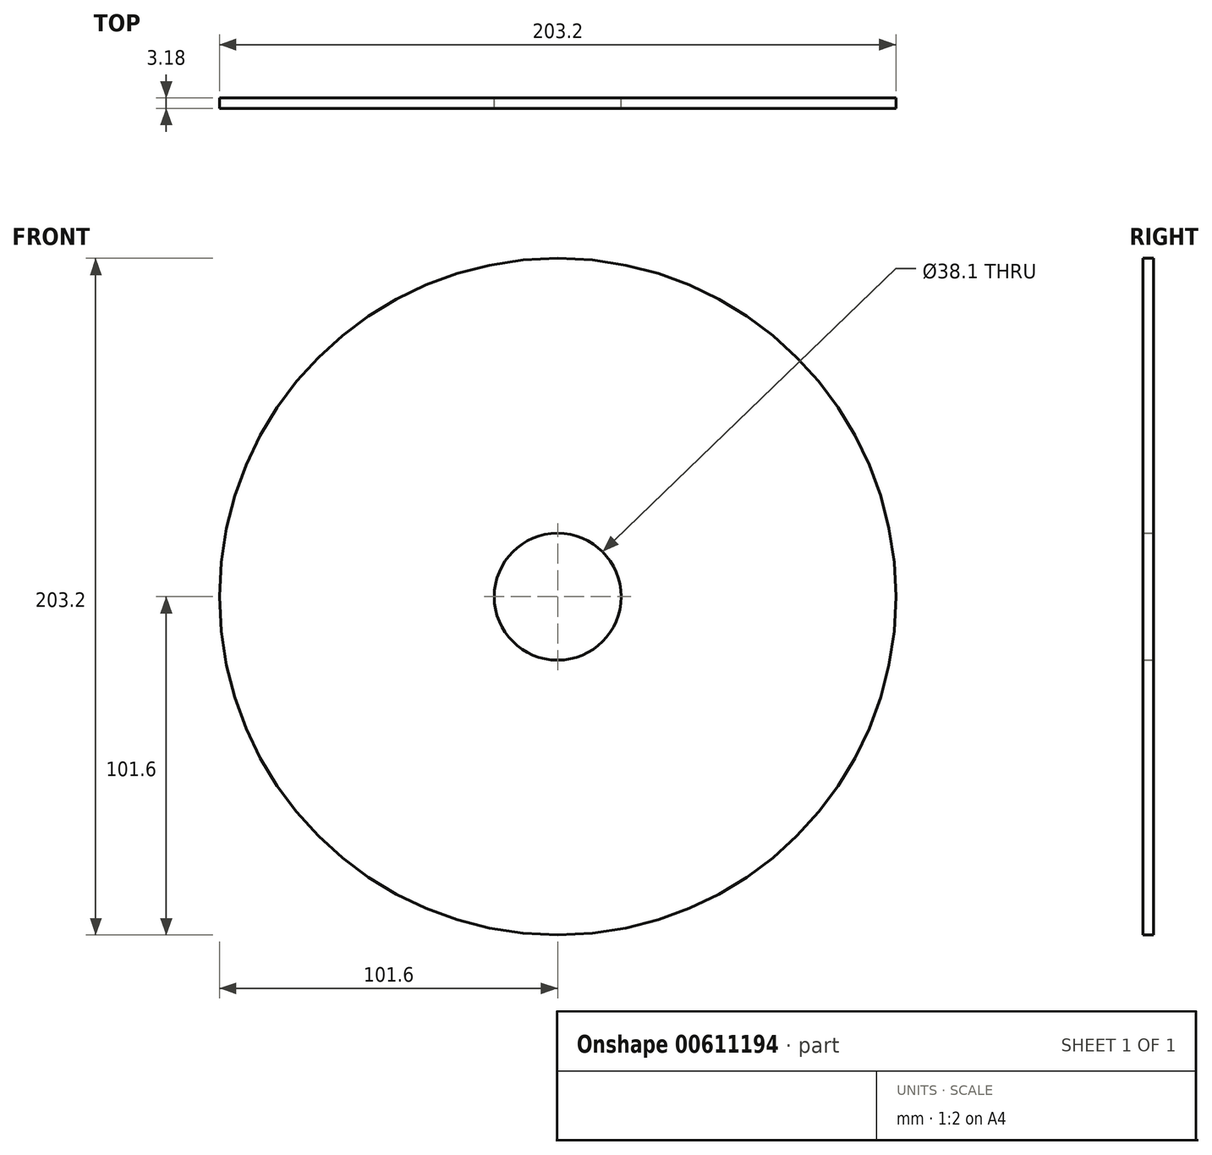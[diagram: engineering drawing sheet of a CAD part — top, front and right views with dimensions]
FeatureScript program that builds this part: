
annotation { "Feature Type Name" : "Feature", "Feature Type Description" : "" }
export const myFeature = defineFeature(function(context is Context, id is Id, definition is map)
    precondition{}
    {
        {
            var Q0;
            Q0=qCreatedBy(makeId("Front.planeOp"),FACE);
            var sketch = newSketch(context, id + "F0", { "sketchPlane" : qUnion([Q0])});
            skCircle(sketch, "E0", {"center": v(0, 0) * mm, "radius": 101.6 * mm});
            skCircle(sketch, "E1", {"center": v(0, 0) * mm, "radius": 19.05 * mm});
            skSolve(sketch);
        }
        {
            var Q0;
            Q0 = qSketchRegion(id + "F0", true);
            extrude(context, id + "F1", {"entities" : qUnion([Q0]), "depth" : 3.17 * mm, "offsetDistance" : 25.4 * mm});
        }
    });
